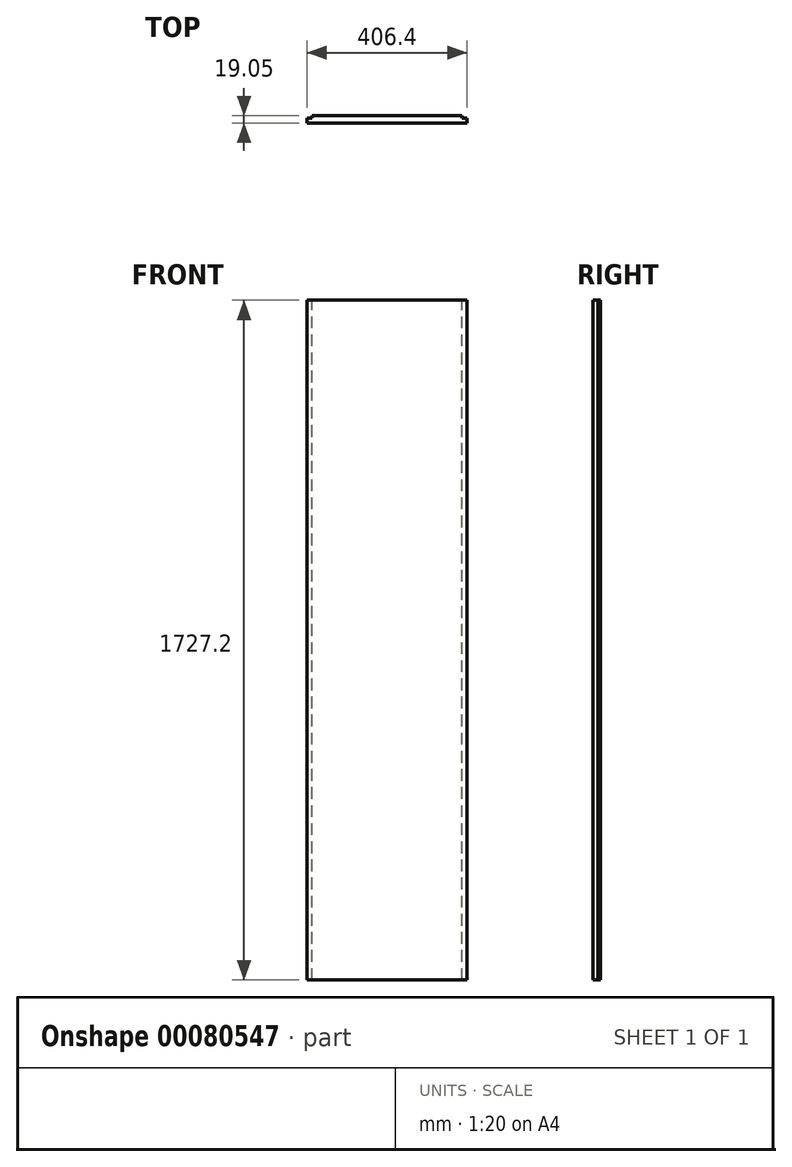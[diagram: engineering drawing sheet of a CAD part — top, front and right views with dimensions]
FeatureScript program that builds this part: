
annotation { "Feature Type Name" : "Feature", "Feature Type Description" : "" }
export const myFeature = defineFeature(function(context is Context, id is Id, definition is map)
    precondition{}
    {
        {
            var Q0;
            Q0=qCreatedBy(makeId("Top.planeOp"),FACE);
            var sketch = newSketch(context, id + "F0", { "sketchPlane" : qUnion([Q0])});
            skLineSegment(sketch, "E0.bottom", {"start": v(-173.48, 0) * mm, "end": v(232.92, 0) * mm});
            skLineSegment(sketch, "E0.top", {"start": v(-173.48, -19.05) * mm, "end": v(232.92, -19.05) * mm});
            skLineSegment(sketch, "E0.left", {"start": v(-173.48, 0) * mm, "end": v(-173.48, -19.05) * mm});
            skLineSegment(sketch, "E0.right", {"start": v(232.92, 0) * mm, "end": v(232.92, -19.05) * mm});
            skSolve(sketch);
        }
        {
            var Q0;
            Q0 = qSketchRegion(id + "F0", true);
            extrude(context, id + "F1", {"entities" : qUnion([Q0]), "depth" : 1727.2 * mm});
        }
        {
            var Q0;
            Q0=makeQuery(id+"F1.opExtrude","CAP_FACE",FACE,{"disambiguationData":[OSD([sQuery(id+"F0.wireOp",EDGE,"E0.bottom"),sQuery(id+"F0.wireOp",EDGE,"E0.top"),sQuery(id+"F0.wireOp",EDGE,"E0.left"),sQuery(id+"F0.wireOp",EDGE,"E0.right")])],"isStart":false});
            var sketch = newSketch(context, id + "F2", { "sketchPlane" : qUnion([Q0])});
            skLineSegment(sketch, "E1", {"start": v(232.92, -6.35) * mm, "end": v(220.22, -6.35) * mm});
            skLineSegment(sketch, "E2", {"start": v(220.22, -6.35) * mm, "end": v(220.22, 0) * mm});
            skSolve(sketch);
        }
        {
            var Q0;
            {var subQ0=sQuery(id+"F2.wireOp",EDGE,"E1");Q0=makeQuery(id+"F2.imprint","IMPRINT",FACE,{"disambiguationData":[TD([[makeQuery(id+"F2.imprint","IMPRINT",EDGE,{"derivedFrom":subQ0}),-1.0]])]});}
            var Q1;
            Q1=makeQuery(id+"F1.opExtrude","CAP_FACE",FACE,{"disambiguationData":[OSD([sQuery(id+"F0.wireOp",EDGE,"E0.bottom"),sQuery(id+"F0.wireOp",EDGE,"E0.top"),sQuery(id+"F0.wireOp",EDGE,"E0.left"),sQuery(id+"F0.wireOp",EDGE,"E0.right")])],"isStart":true});
            extrude(context, id + "F3", {"entities" : qUnion([Q0, Q1]), "operationType" : NewBodyOperationType.REMOVE, "endBound" : BoundingType.THROUGH_ALL, "oppositeDirection" : true, "depth" : 25.4 * mm});
        }
        {
            var Q0;
            Q0=makeQuery(id+"F1.opExtrude","CAP_FACE",FACE,{"disambiguationData":[OSD([sQuery(id+"F0.wireOp",EDGE,"E0.bottom"),sQuery(id+"F0.wireOp",EDGE,"E0.top"),sQuery(id+"F0.wireOp",EDGE,"E0.left"),sQuery(id+"F0.wireOp",EDGE,"E0.right")])],"isStart":false});
            var sketch = newSketch(context, id + "F4", { "sketchPlane" : qUnion([Q0])});
            skLineSegment(sketch, "E3", {"start": v(-173.48, -6.35) * mm, "end": v(-160.78, -6.35) * mm});
            skLineSegment(sketch, "E4", {"start": v(-160.78, -6.35) * mm, "end": v(-160.78, 0) * mm});
            skSolve(sketch);
        }
        {
            var Q0;
            {var subQ0=sQuery(id+"F4.wireOp",EDGE,"E3");Q0=makeQuery(id+"F4.imprint","IMPRINT",FACE,{"disambiguationData":[TD([[makeQuery(id+"F4.imprint","IMPRINT",EDGE,{"derivedFrom":subQ0}),1.0]])]});}
            extrude(context, id + "F5", {"entities" : qUnion([Q0]), "operationType" : NewBodyOperationType.REMOVE, "endBound" : BoundingType.THROUGH_ALL, "oppositeDirection" : true, "depth" : 25.4 * mm});
        }
    });
